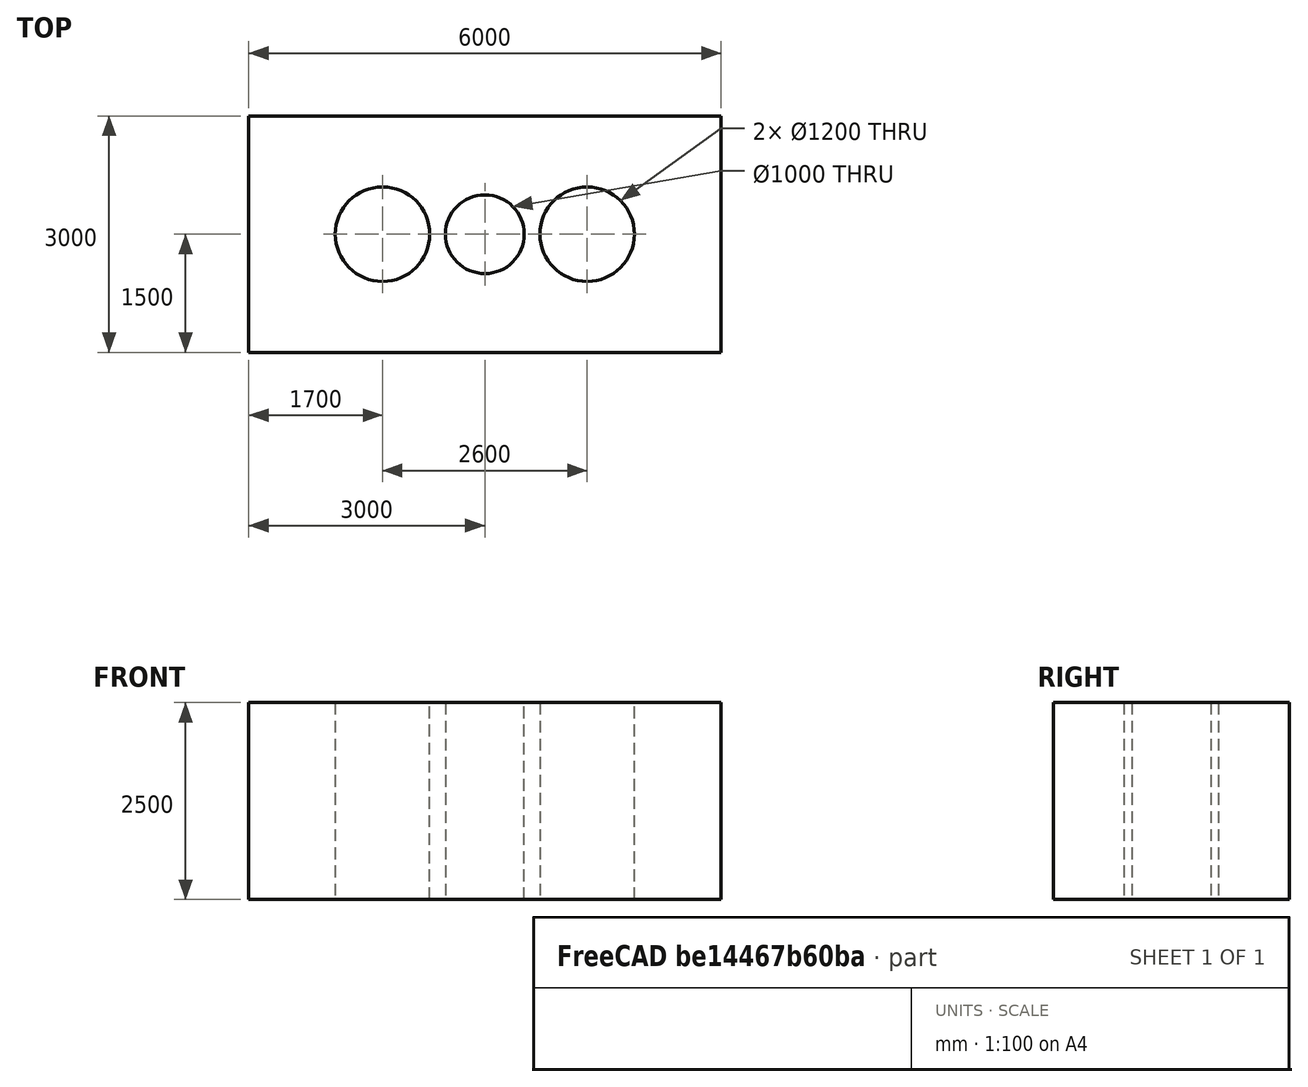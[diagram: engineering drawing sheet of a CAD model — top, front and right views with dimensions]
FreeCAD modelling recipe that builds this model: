
FCSTD DOCUMENT  (FreeCAD 1.0R39109 (Git))
Label: вент блок
License: All rights reserved
LicenseURL: https://en.wikipedia.org/wiki/All_rights_reserved
objects: Sketcher::SketchObject×1, PartDesign::Pad×1, PartDesign::Body×1
note: 6 computed .brp shape members not serialized (recipe doc carries the construction recipe); baked Part::Feature solids carry a one-line shape summary decoded from their .brp

FEATURE [Sketcher::SketchObject] Sketch
  ArcFitTolerance = 1e-06
  AttachmentSupport = -> [XY_Plane]
  FullyConstrained = true
  MakeInternals = false
  MapMode = 5
  sketch-geometry (7):
    g0: LineSegment StartX=0 StartY=0 StartZ=0 EndX=0 EndY=-3000 EndZ=0
    g1: LineSegment StartX=0 StartY=-3000 StartZ=0 EndX=6000 EndY=-3000 EndZ=0
    g2: LineSegment StartX=6000 StartY=-3000 StartZ=0 EndX=6000 EndY=0 EndZ=0
    g3: LineSegment StartX=6000 StartY=0 StartZ=0 EndX=0 EndY=0 EndZ=0
    g4: Circle CenterX=1700 CenterY=-1500 CenterZ=0 NormalX=0 NormalY=0 NormalZ=1 AngleXU=0 Radius=600
    g5: Circle CenterX=4300 CenterY=-1500 CenterZ=0 NormalX=0 NormalY=0 NormalZ=1 AngleXU=0 Radius=600
    g6: Circle CenterX=3000 CenterY=-1500 CenterZ=0 NormalX=0 NormalY=0 NormalZ=1 AngleXU=0 Radius=500
  constraints (20):
    c: Coincident(g0,g1)
    c: Coincident(g1,g2)
    c: Coincident(g2,g3)
    c: Coincident(g3,g0)
    c: Vertical(g0)
    c: Vertical(g2)
    c: Horizontal(g1)
    c: Horizontal(g3)
    c: Distance(g0,g2) = 6000
    c: Distance(g1,g3) = 3000
    c: Coincident(g0,g-1)
    c: Diameter(g4) = 1200
    c: Diameter(g5) = 1200
    c: Distance(g5,g2) = 1100
    c: Distance(g4,g0) = 1100
    c: Distance(g5,g3) = 1500
    c: Distance(g4,g3) = 1500
    c: Diameter(g6) = 1000
    c: Distance(g6,g2) = 3000
    c: Distance(g6,g1) = 1500
FEATURE [PartDesign::Pad] Pad
  Direction = (0,0,1)
  Length = 2500
  Length2 = 10
  Profile = -> Sketch
  ReferenceAxis = -> Sketch [N_Axis]
  Refine = true
  Suppressed = false
  Type = 0
FEATURE [PartDesign::Body] Body  label="Тело"
  AllowCompound = false
  Group = -> [Sketch,Pad]
  Origin = -> Origin
  Tip = -> Pad
